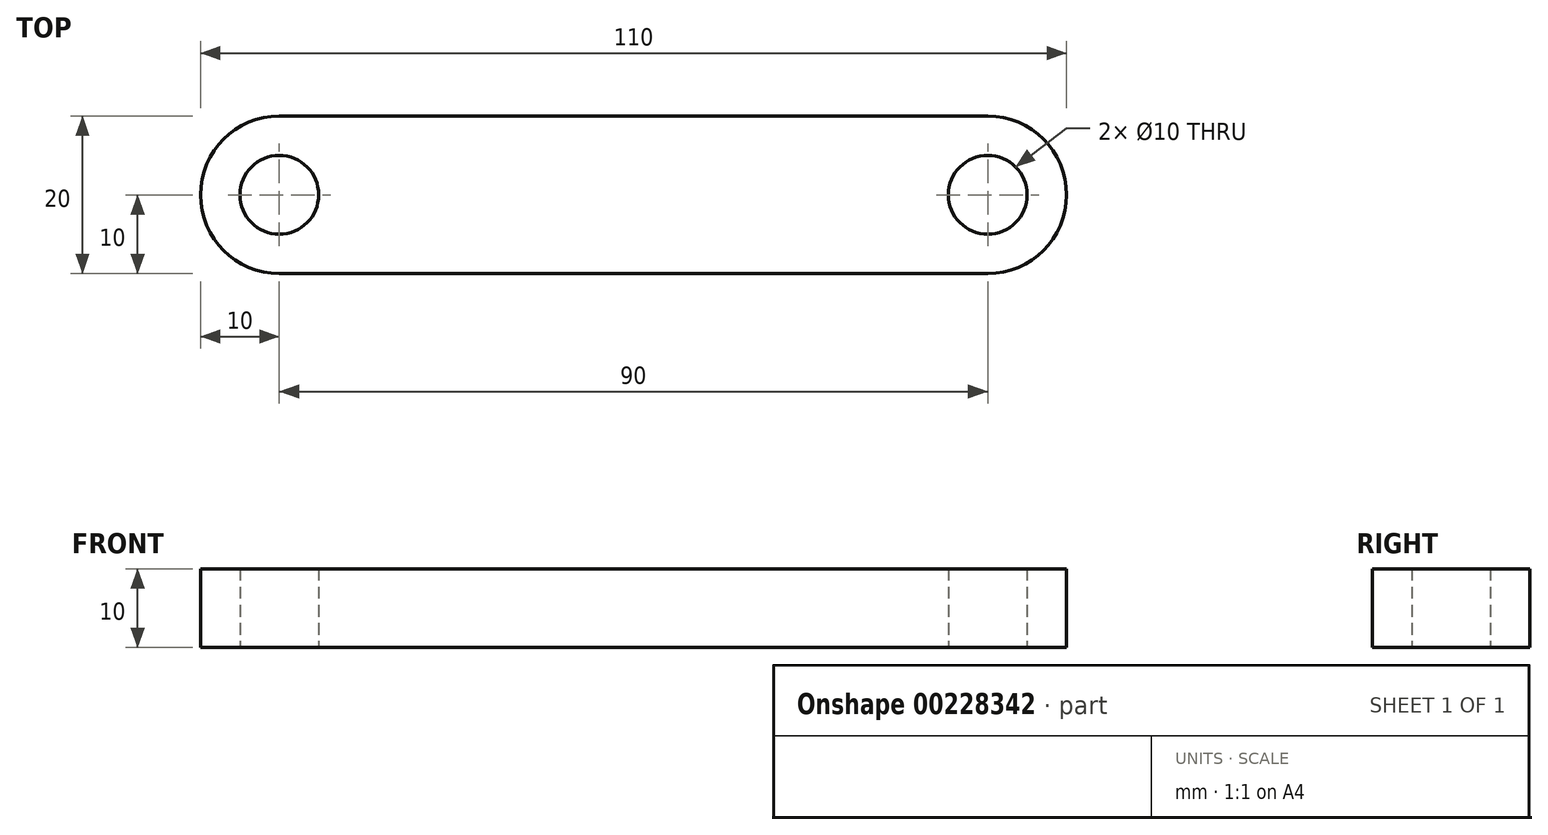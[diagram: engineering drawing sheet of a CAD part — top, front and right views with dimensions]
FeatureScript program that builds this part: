
annotation { "Feature Type Name" : "Feature", "Feature Type Description" : "" }
export const myFeature = defineFeature(function(context is Context, id is Id, definition is map)
    precondition{}
    {
        {
            var Q0;
            Q0=qCreatedBy(makeId("Top.planeOp"),FACE);
            var sketch = newSketch(context, id + "F0", { "sketchPlane" : qUnion([Q0])});
            skLineSegment(sketch, "E0.bottom", {"start": v(45, 10) * mm, "end": v(-45, 10) * mm});
            skLineSegment(sketch, "E0.top", {"start": v(45, -10) * mm, "end": v(-45, -10) * mm});
            skLineSegment(sketch, "E0.left", {"start": v(55, 0) * mm, "end": v(55, 0) * mm});
            skLineSegment(sketch, "E0.right", {"start": v(-55, 0) * mm, "end": v(-55, 0) * mm});
            skPoint(sketch, "E0.middle", {"position": v(0, 0) * mm});
            skPoint(sketch, "E1.visualSharp", {"position": v(55, -10) * mm});
            skArc(sketch, "E1.filletArc", {"start": v(45, -10) * mm, "mid": v(52.07, -7.07) * mm, "end": v(55, 0) * mm});
            skPoint(sketch, "E2.visualSharp", {"position": v(55, 10) * mm});
            skArc(sketch, "E2.filletArc", {"start": v(55, 0) * mm, "mid": v(52.07, 7.07) * mm, "end": v(45, 10) * mm});
            skPoint(sketch, "E3.visualSharp", {"position": v(-55, -10) * mm});
            skArc(sketch, "E3.filletArc", {"start": v(-55, 0) * mm, "mid": v(-52.07, -7.07) * mm, "end": v(-45, -10) * mm});
            skPoint(sketch, "E4.visualSharp", {"position": v(-55, 10) * mm});
            skArc(sketch, "E4.filletArc", {"start": v(-45, 10) * mm, "mid": v(-52.07, 7.07) * mm, "end": v(-55, 0) * mm});
            skCircle(sketch, "E5", {"center": v(-45, 0) * mm, "radius": 5 * mm});
            skCircle(sketch, "E6", {"center": v(45, 0) * mm, "radius": 5 * mm});
            skSolve(sketch);
        }
        {
            var Q0;
            Q0=makeQuery(id+"F0.imprint","IMPRINT",FACE,{"disambiguationData":[TD([[makeQuery(id+"F0.imprint","IMPRINT",EDGE,{"derivedFrom":sQuery(id+"F0.wireOp",EDGE,"E0.bottom")}),1.0]])]});
            extrude(context, id + "F1", {"entities" : qUnion([Q0]), "depth" : 10 * mm});
        }
    });
